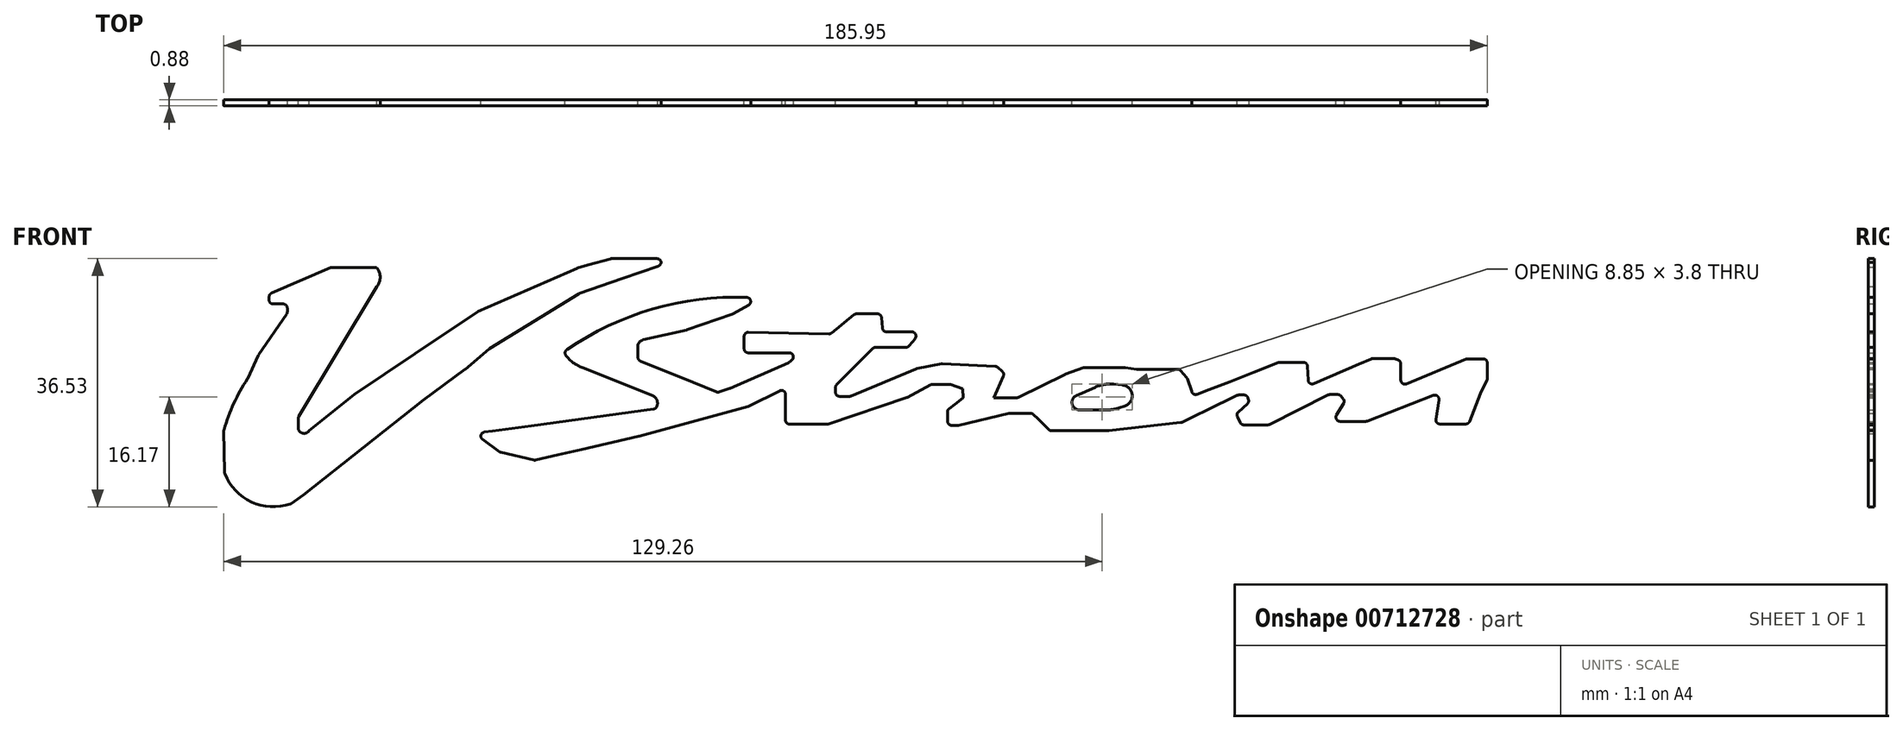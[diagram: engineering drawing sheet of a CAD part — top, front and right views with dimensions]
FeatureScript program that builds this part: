
annotation { "Feature Type Name" : "Feature", "Feature Type Description" : "" }
export const myFeature = defineFeature(function(context is Context, id is Id, definition is map)
    precondition{}
    {
        {
            var Q0;
            Q0=qCreatedBy(makeId("Front.planeOp"),FACE);
            var sketch = newSketch(context, id + "F0", { "sketchPlane" : qUnion([Q0])});
            skLineSegment(sketch, "E0", {"start": v(71.75, 23.37) * mm, "end": v(68, 21.28) * mm});
            skLineSegment(sketch, "E1", {"start": v(68, 21.28) * mm, "end": v(61.86, 19.14) * mm});
            skLineSegment(sketch, "E2", {"start": v(61.86, 19.14) * mm, "end": v(56.05, 17.82) * mm});
            skLineSegment(sketch, "E3", {"start": v(55.28, 16.82) * mm, "end": v(55.32, 15.1) * mm});
            skLineSegment(sketch, "E4", {"start": v(55.32, 15.1) * mm, "end": v(62.67, 12.12) * mm});
            skLineSegment(sketch, "E5", {"start": v(62.67, 12.12) * mm, "end": v(66, 10.76) * mm});
            skLineSegment(sketch, "E6", {"start": v(66, 10.76) * mm, "end": v(67.6, 11.32) * mm});
            skLineSegment(sketch, "E7", {"start": v(67.6, 11.32) * mm, "end": v(75.53, 14.78) * mm});
            skLineSegment(sketch, "E8", {"start": v(75.53, 14.78) * mm, "end": v(77.05, 16.07) * mm});
            skLineSegment(sketch, "E9", {"start": v(77.05, 16.07) * mm, "end": v(69.52, 16.07) * mm});
            skLineSegment(sketch, "E10", {"start": v(69.52, 16.07) * mm, "end": v(69.52, 18.83) * mm});
            skLineSegment(sketch, "E11", {"start": v(69.52, 18.83) * mm, "end": v(81.09, 18.6) * mm});
            skLineSegment(sketch, "E12", {"start": v(81.09, 18.6) * mm, "end": v(84.4, 21.29) * mm});
            skLineSegment(sketch, "E13", {"start": v(84.4, 21.29) * mm, "end": v(87.87, 21.29) * mm});
            skLineSegment(sketch, "E14", {"start": v(87.87, 21.29) * mm, "end": v(88.07, 18.87) * mm});
            skLineSegment(sketch, "E15", {"start": v(88.07, 18.87) * mm, "end": v(93.1, 18.87) * mm});
            skLineSegment(sketch, "E16", {"start": v(93.1, 18.87) * mm, "end": v(91.44, 16.8) * mm});
            skLineSegment(sketch, "E17", {"start": v(91.44, 16.8) * mm, "end": v(86.88, 16.8) * mm});
            skLineSegment(sketch, "E18", {"start": v(86.88, 16.8) * mm, "end": v(81.75, 11.67) * mm});
            skLineSegment(sketch, "E19", {"start": v(81.75, 11.67) * mm, "end": v(81.75, 10.24) * mm});
            skLineSegment(sketch, "E20", {"start": v(81.75, 10.24) * mm, "end": v(83.7, 10.24) * mm});
            skLineSegment(sketch, "E21", {"start": v(83.7, 10.24) * mm, "end": v(92.6, 13.94) * mm});
            skLineSegment(sketch, "E22", {"start": v(92.6, 13.94) * mm, "end": v(95.98, 14.63) * mm});
            skLineSegment(sketch, "E23", {"start": v(95.98, 14.63) * mm, "end": v(103.29, 14.27) * mm});
            skLineSegment(sketch, "E24", {"start": v(103.29, 14.27) * mm, "end": v(104.36, 13.3) * mm});
            skLineSegment(sketch, "E25", {"start": v(104.36, 13.3) * mm, "end": v(103.4, 11.1) * mm});
            skLineSegment(sketch, "E26", {"start": v(103.4, 11.1) * mm, "end": v(102.94, 10.06) * mm});
            skLineSegment(sketch, "E27", {"start": v(102.94, 10.06) * mm, "end": v(103.99, 10.06) * mm});
            skLineSegment(sketch, "E28", {"start": v(103.99, 10.06) * mm, "end": v(106.08, 10.06) * mm});
            skLineSegment(sketch, "E29", {"start": v(106.08, 10.06) * mm, "end": v(112.49, 13.2) * mm});
            skLineSegment(sketch, "E30", {"start": v(112.49, 13.2) * mm, "end": v(115.03, 14.1) * mm});
            skLineSegment(sketch, "E31", {"start": v(115.03, 14.1) * mm, "end": v(118.01, 14.1) * mm});
            skLineSegment(sketch, "E32", {"start": v(118.01, 14.1) * mm, "end": v(120.48, 14.1) * mm});
            skLineSegment(sketch, "E33", {"start": v(120.48, 14.1) * mm, "end": v(122.09, 13.88) * mm});
            skLineSegment(sketch, "E34", {"start": v(-35.24, 14.16) * mm, "end": v(-35.24, 14.16) * mm});
            skLineSegment(sketch, "E35", {"start": v(122.09, 13.88) * mm, "end": v(127.78, 13.88) * mm});
            skLineSegment(sketch, "E36", {"start": v(127.78, 13.88) * mm, "end": v(128.8, 12.7) * mm});
            skLineSegment(sketch, "E37", {"start": v(128.8, 12.7) * mm, "end": v(129.41, 10.9) * mm});
            skLineSegment(sketch, "E38", {"start": v(129.41, 10.9) * mm, "end": v(129.41, 10.23) * mm});
            skLineSegment(sketch, "E39", {"start": v(129.41, 10.23) * mm, "end": v(131.71, 11.13) * mm});
            skLineSegment(sketch, "E40", {"start": v(131.71, 11.13) * mm, "end": v(134.48, 12.2) * mm});
            skLineSegment(sketch, "E41", {"start": v(134.48, 12.2) * mm, "end": v(137.66, 13.45) * mm});
            skLineSegment(sketch, "E42", {"start": v(137.66, 13.45) * mm, "end": v(141.15, 14.8) * mm});
            skLineSegment(sketch, "E43", {"start": v(141.15, 14.8) * mm, "end": v(144.88, 14.8) * mm});
            skLineSegment(sketch, "E44", {"start": v(144.88, 14.8) * mm, "end": v(145, 12.25) * mm});
            skLineSegment(sketch, "E45", {"start": v(145, 12.25) * mm, "end": v(145.02, 11.64) * mm});
            skLineSegment(sketch, "E46", {"start": v(145.02, 11.64) * mm, "end": v(151.78, 14.55) * mm});
            skLineSegment(sketch, "E47", {"start": v(151.78, 14.55) * mm, "end": v(153.53, 15.3) * mm});
            skLineSegment(sketch, "E48", {"start": v(153.53, 15.3) * mm, "end": v(156.55, 15.3) * mm});
            skLineSegment(sketch, "E49", {"start": v(156.55, 15.3) * mm, "end": v(157.39, 14.97) * mm});
            skLineSegment(sketch, "E50", {"start": v(157.39, 14.97) * mm, "end": v(157.39, 12.95) * mm});
            skLineSegment(sketch, "E51", {"start": v(157.39, 12.95) * mm, "end": v(157.39, 12.28) * mm});
            skLineSegment(sketch, "E52", {"start": v(157.39, 12.28) * mm, "end": v(157.39, 11.6) * mm});
            skLineSegment(sketch, "E53", {"start": v(157.39, 11.6) * mm, "end": v(166.26, 15.27) * mm});
            skLineSegment(sketch, "E54", {"start": v(166.26, 15.27) * mm, "end": v(168.95, 15.27) * mm});
            skLineSegment(sketch, "E55", {"start": v(168.95, 15.27) * mm, "end": v(168.95, 12.49) * mm});
            skLineSegment(sketch, "E56", {"start": v(168.95, 12.49) * mm, "end": v(168.03, 10.64) * mm});
            skLineSegment(sketch, "E57", {"start": v(8.4, 22.6) * mm, "end": v(8.4, 21.37) * mm});
            skLineSegment(sketch, "E58", {"start": v(8.4, 21.37) * mm, "end": v(4.54, 15.76) * mm});
            skLineSegment(sketch, "E59", {"start": v(4.54, 15.76) * mm, "end": v(3.07, 12.62) * mm});
            skLineSegment(sketch, "E60", {"start": v(9.86, 7.43) * mm, "end": v(9.86, 5.91) * mm});
            skArc(sketch, "E61", {"start": v(9.86, 6.28) * mm, "mid": v(10.32, 5.35) * mm, "end": v(11.32, 5.64) * mm});
            skLineSegment(sketch, "E62", {"start": v(11.32, 5.64) * mm, "end": v(17.38, 10.52) * mm});
            skLineSegment(sketch, "E63", {"start": v(17.38, 10.52) * mm, "end": v(25.44, 15.92) * mm});
            skLineSegment(sketch, "E64", {"start": v(25.44, 15.92) * mm, "end": v(33.85, 21.57) * mm});
            skLineSegment(sketch, "E65", {"start": v(33.85, 21.57) * mm, "end": v(47.2, 27.4) * mm});
            skLineSegment(sketch, "E66", {"start": v(47.2, 27.4) * mm, "end": v(48.62, 27.8) * mm});
            skLineSegment(sketch, "E67", {"start": v(48.62, 27.8) * mm, "end": v(51.72, 28.68) * mm});
            skLineSegment(sketch, "E68", {"start": v(51.72, 28.68) * mm, "end": v(58.4, 28.68) * mm});
            skLineSegment(sketch, "E69", {"start": v(58.4, 28.68) * mm, "end": v(58.4, 27.8) * mm});
            skLineSegment(sketch, "E70", {"start": v(58.4, 27.8) * mm, "end": v(53.3, 26.05) * mm});
            skLineSegment(sketch, "E71", {"start": v(53.3, 26.05) * mm, "end": v(47.42, 24.02) * mm});
            skLineSegment(sketch, "E72", {"start": v(47.42, 24.02) * mm, "end": v(35.42, 16.61) * mm});
            skLineSegment(sketch, "E73", {"start": v(35.42, 16.61) * mm, "end": v(32.2, 13.86) * mm});
            skLineSegment(sketch, "E74", {"start": v(33.43, 5.28) * mm, "end": v(35.83, 5.6) * mm});
            skLineSegment(sketch, "E75", {"start": v(5.96, 22.6) * mm, "end": v(5.96, 23.91) * mm});
            skLineSegment(sketch, "E76", {"start": v(5.96, 23.91) * mm, "end": v(14.33, 27.5) * mm});
            skLineSegment(sketch, "E77", {"start": v(14.33, 27.5) * mm, "end": v(20.37, 27.5) * mm});
            skLineSegment(sketch, "E78", {"start": v(20.4, 24.92) * mm, "end": v(9.86, 7.43) * mm});
            skLineSegment(sketch, "E79", {"start": v(5.96, 22.6) * mm, "end": v(8.4, 22.6) * mm});
            skArc(sketch, "E80", {"start": v(20.4, 24.92) * mm, "mid": v(20.82, 26.21) * mm, "end": v(20.37, 27.5) * mm});
            skLineSegment(sketch, "E81", {"start": v(57.34, 10.31) * mm, "end": v(47.91, 14.1) * mm});
            skArc(sketch, "E82", {"start": v(45.36, 16.2) * mm, "mid": v(46.45, 14.92) * mm, "end": v(47.91, 14.1) * mm});
            skArc(sketch, "E83", {"start": v(57.64, 8.58) * mm, "mid": v(57.89, 9.64) * mm, "end": v(57.12, 10.4) * mm});
            skLineSegment(sketch, "E84", {"start": v(166.46, 6.55) * mm, "end": v(161.99, 6.55) * mm});
            skLineSegment(sketch, "E85", {"start": v(161.99, 6.55) * mm, "end": v(162.63, 10.72) * mm});
            skLineSegment(sketch, "E86", {"start": v(162.63, 10.72) * mm, "end": v(152.81, 6.9) * mm});
            skLineSegment(sketch, "E87", {"start": v(152.81, 6.9) * mm, "end": v(148.28, 6.9) * mm});
            skLineSegment(sketch, "E88", {"start": v(148.28, 6.9) * mm, "end": v(149.93, 9.6) * mm});
            skLineSegment(sketch, "E89", {"start": v(149.93, 9.6) * mm, "end": v(149.22, 10.48) * mm});
            skLineSegment(sketch, "E90", {"start": v(149.22, 10.48) * mm, "end": v(147.75, 10.48) * mm});
            skLineSegment(sketch, "E91", {"start": v(147.75, 10.48) * mm, "end": v(139.7, 6.43) * mm});
            skLineSegment(sketch, "E92", {"start": v(139.7, 6.43) * mm, "end": v(136.05, 6.43) * mm});
            skLineSegment(sketch, "E93", {"start": v(136.05, 6.43) * mm, "end": v(135.34, 7.9) * mm});
            skLineSegment(sketch, "E94", {"start": v(135.34, 7.9) * mm, "end": v(137.1, 9.49) * mm});
            skLineSegment(sketch, "E95", {"start": v(137.1, 9.49) * mm, "end": v(136.82, 10.43) * mm});
            skLineSegment(sketch, "E96", {"start": v(136.82, 10.43) * mm, "end": v(135.61, 10.43) * mm});
            skLineSegment(sketch, "E97", {"start": v(135.61, 10.43) * mm, "end": v(131.41, 8.4) * mm});
            skLineSegment(sketch, "E98", {"start": v(131.41, 8.4) * mm, "end": v(129.95, 7.68) * mm});
            skLineSegment(sketch, "E99", {"start": v(129.95, 7.68) * mm, "end": v(128.02, 6.75) * mm});
            skLineSegment(sketch, "E100", {"start": v(128.02, 6.75) * mm, "end": v(121.39, 6) * mm});
            skLineSegment(sketch, "E101", {"start": v(121.39, 6) * mm, "end": v(118.26, 5.64) * mm});
            skLineSegment(sketch, "E102", {"start": v(118.26, 5.64) * mm, "end": v(112.75, 5.64) * mm});
            skLineSegment(sketch, "E103", {"start": v(112.75, 5.64) * mm, "end": v(110.45, 5.64) * mm});
            skLineSegment(sketch, "E104", {"start": v(110.45, 5.64) * mm, "end": v(108.8, 7.27) * mm});
            skLineSegment(sketch, "E105", {"start": v(108.8, 7.27) * mm, "end": v(108.1, 7.96) * mm});
            skLineSegment(sketch, "E106", {"start": v(108.1, 7.96) * mm, "end": v(107.3, 7.96) * mm});
            skLineSegment(sketch, "E107", {"start": v(107.3, 7.96) * mm, "end": v(105.01, 7.96) * mm});
            skLineSegment(sketch, "E108", {"start": v(105.01, 7.96) * mm, "end": v(98.13, 6.37) * mm});
            skLineSegment(sketch, "E109", {"start": v(98.13, 6.37) * mm, "end": v(96.74, 6.37) * mm});
            skLineSegment(sketch, "E110", {"start": v(96.74, 6.37) * mm, "end": v(96.74, 8.45) * mm});
            skLineSegment(sketch, "E111", {"start": v(96.74, 8.45) * mm, "end": v(97.7, 9.2) * mm});
            skLineSegment(sketch, "E112", {"start": v(97.7, 9.2) * mm, "end": v(98.82, 10.04) * mm});
            skLineSegment(sketch, "E113", {"start": v(98.82, 10.04) * mm, "end": v(98.77, 11.27) * mm});
            skLineSegment(sketch, "E114", {"start": v(98.77, 11.27) * mm, "end": v(97.06, 11.86) * mm});
            skLineSegment(sketch, "E115", {"start": v(97.06, 11.86) * mm, "end": v(94.56, 11.86) * mm});
            skLineSegment(sketch, "E116", {"start": v(94.56, 11.86) * mm, "end": v(91.36, 10.1) * mm});
            skLineSegment(sketch, "E117", {"start": v(91.36, 10.1) * mm, "end": v(80.65, 6.52) * mm});
            skLineSegment(sketch, "E118", {"start": v(80.65, 6.52) * mm, "end": v(77.45, 6.52) * mm});
            skLineSegment(sketch, "E119", {"start": v(77.45, 6.52) * mm, "end": v(75.05, 6.52) * mm});
            skLineSegment(sketch, "E120", {"start": v(75.05, 6.52) * mm, "end": v(75.05, 11.05) * mm});
            skLineSegment(sketch, "E121", {"start": v(75.05, 11.05) * mm, "end": v(74.4, 11.05) * mm});
            skLineSegment(sketch, "E122", {"start": v(74.4, 11.05) * mm, "end": v(70.14, 8.92) * mm});
            skLineSegment(sketch, "E123", {"start": v(70.14, 8.92) * mm, "end": v(55.44, 4.9) * mm});
            skLineSegment(sketch, "E124", {"start": v(55.44, 4.9) * mm, "end": v(47.76, 3.13) * mm});
            skLineSegment(sketch, "E125", {"start": v(47.76, 3.13) * mm, "end": v(44.61, 2.4) * mm});
            skLineSegment(sketch, "E126", {"start": v(44.61, 2.4) * mm, "end": v(41.52, 1.69) * mm});
            skLineSegment(sketch, "E127", {"start": v(41.52, 1.69) * mm, "end": v(36.86, 2.77) * mm});
            skLineSegment(sketch, "E128", {"start": v(36.86, 2.77) * mm, "end": v(33.43, 5.28) * mm});
            skLineSegment(sketch, "E129", {"start": v(-0.1, 5.7) * mm, "end": v(0, 0) * mm});
            skLineSegment(sketch, "E130", {"start": v(26.6, 9.77) * mm, "end": v(10.57, -2.96) * mm});
            skLineSegment(sketch, "E131", {"start": v(10.57, -2.96) * mm, "end": v(8.9, -4.11) * mm});
            skLineSegment(sketch, "E132", {"start": v(41.05, 6.32) * mm, "end": v(57.64, 8.58) * mm});
            skLineSegment(sketch, "E133", {"start": v(168.03, 10.64) * mm, "end": v(166.46, 6.55) * mm});
            skArc(sketch, "E134", {"start": v(3.07, 12.62) * mm, "mid": v(1.23, 9.28) * mm, "end": v(-0.1, 5.7) * mm});
            skLineSegment(sketch, "E135", {"start": v(32.2, 13.86) * mm, "end": v(26.6, 9.77) * mm});
            skLineSegment(sketch, "E136", {"start": v(41.05, 6.32) * mm, "end": v(35.83, 5.6) * mm});
            skArc(sketch, "E137", {"start": v(113.98, 10.35) * mm, "mid": v(113.4, 9.23) * mm, "end": v(114.38, 8.44) * mm});
            skLineSegment(sketch, "E138", {"start": v(113.98, 10.35) * mm, "end": v(116.47, 11.46) * mm});
            skLineSegment(sketch, "E139", {"start": v(114.38, 8.44) * mm, "end": v(118.08, 8.44) * mm});
            skArc(sketch, "E140", {"start": v(120.48, 8.98) * mm, "mid": v(121.44, 10.5) * mm, "end": v(120.14, 11.77) * mm});
            skLineSegment(sketch, "E141", {"start": v(118.97, 11.88) * mm, "end": v(120.14, 11.77) * mm});
            skLineSegment(sketch, "E142", {"start": v(119.72, 8.71) * mm, "end": v(120.48, 8.98) * mm});
            skPoint(sketch, "E143.visualSharp", {"position": v(117.67, 12) * mm});
            skArc(sketch, "E143.filletArc", {"start": v(118.97, 11.88) * mm, "mid": v(117.7, 11.83) * mm, "end": v(116.47, 11.46) * mm});
            skPoint(sketch, "E144.visualSharp", {"position": v(118.92, 8.44) * mm});
            skArc(sketch, "E144.filletArc", {"start": v(118.08, 8.44) * mm, "mid": v(118.91, 8.5) * mm, "end": v(119.72, 8.71) * mm});
            skArc(sketch, "E145", {"start": v(71.75, 23.37) * mm, "mid": v(57.92, 22.11) * mm, "end": v(45.36, 16.2) * mm});
            skPoint(sketch, "E146.visualSharp", {"position": v(55.25, 17.64) * mm});
            skArc(sketch, "E146.filletArc", {"start": v(56.05, 17.82) * mm, "mid": v(55.49, 17.46) * mm, "end": v(55.28, 16.82) * mm});
            skArc(sketch, "E147", {"start": v(0, 0) * mm, "mid": v(3.6, -3.89) * mm, "end": v(8.9, -4.11) * mm});
            skSolve(sketch);
        }
        {
            var Q0;
            Q0=qSketchRegion(id+"F0",true);
            extrude(context, id + "F1", {"entities" : qUnion([Q0]), "depth" : .8 * mm, "offsetDistance" : 25 * mm});
        }
        {
            var Q0;
            Q0=makeQuery(id+"F1.opExtrude","SWEPT_BODY",BODY,{"disambiguationData":[OSD([sQuery(id+"F0.wireOp",EDGE,"241e14e1-87a1-43d8-a896-4ed85162aa12"),sQuery(id+"F0.wireOp",EDGE,"f7f46965-fdce-40b1-8a69-0ea02161d450"),sQuery(id+"F0.wireOp",EDGE,"a256f486-1147-4e8e-9624-e69cd99640f2"),sQuery(id+"F0.wireOp",EDGE,"E0"),sQuery(id+"F0.wireOp",EDGE,"E1"),sQuery(id+"F0.wireOp",EDGE,"E2"),sQuery(id+"F0.wireOp",EDGE,"E3"),sQuery(id+"F0.wireOp",EDGE,"E4"),sQuery(id+"F0.wireOp",EDGE,"E5"),sQuery(id+"F0.wireOp",EDGE,"E6"),sQuery(id+"F0.wireOp",EDGE,"E7"),sQuery(id+"F0.wireOp",EDGE,"E8"),sQuery(id+"F0.wireOp",EDGE,"E9"),sQuery(id+"F0.wireOp",EDGE,"E10"),sQuery(id+"F0.wireOp",EDGE,"E11"),sQuery(id+"F0.wireOp",EDGE,"E12"),sQuery(id+"F0.wireOp",EDGE,"E13"),sQuery(id+"F0.wireOp",EDGE,"E14"),sQuery(id+"F0.wireOp",EDGE,"E15"),sQuery(id+"F0.wireOp",EDGE,"E16"),sQuery(id+"F0.wireOp",EDGE,"E17"),sQuery(id+"F0.wireOp",EDGE,"E18"),sQuery(id+"F0.wireOp",EDGE,"E19"),sQuery(id+"F0.wireOp",EDGE,"E20"),sQuery(id+"F0.wireOp",EDGE,"E21"),sQuery(id+"F0.wireOp",EDGE,"E22"),sQuery(id+"F0.wireOp",EDGE,"E23"),sQuery(id+"F0.wireOp",EDGE,"E24"),sQuery(id+"F0.wireOp",EDGE,"E25"),sQuery(id+"F0.wireOp",EDGE,"E26"),sQuery(id+"F0.wireOp",EDGE,"E27"),sQuery(id+"F0.wireOp",EDGE,"E28"),sQuery(id+"F0.wireOp",EDGE,"E29"),sQuery(id+"F0.wireOp",EDGE,"E30"),sQuery(id+"F0.wireOp",EDGE,"E31"),sQuery(id+"F0.wireOp",EDGE,"E32"),sQuery(id+"F0.wireOp",EDGE,"E33"),sQuery(id+"F0.wireOp",EDGE,"24c02880-417f-4c24-b8b8-f4173c506c8a"),sQuery(id+"F0.wireOp",EDGE,"c1167789-1dd6-4c8a-b9db-14aab257ee89"),sQuery(id+"F0.wireOp",EDGE,"97e02e69-64ad-4fc2-ba99-ada5d7f4203f"),sQuery(id+"F0.wireOp",EDGE,"a728134e-6b61-4dc4-b5d7-6c3bc719696b"),sQuery(id+"F0.wireOp",EDGE,"03a7d401-13a4-461c-8d26-49e58f535fc3"),sQuery(id+"F0.wireOp",EDGE,"a3bd3416-707c-4540-b944-4694eed28f36"),sQuery(id+"F0.wireOp",EDGE,"ae496998-b544-44f2-afee-4042db2af114"),sQuery(id+"F0.wireOp",EDGE,"d8a8be79-a09e-4068-9526-32c7dd8d4367"),sQuery(id+"F0.wireOp",EDGE,"6c9cf376-8706-417d-a2f8-7997adb0d334"),sQuery(id+"F0.wireOp",EDGE,"4fed2303-0bfb-4ab1-8d0b-459c1d0f22cc"),sQuery(id+"F0.wireOp",EDGE,"54fe9d9b-3ee6-47e4-8d7e-fb489f7f2c80"),sQuery(id+"F0.wireOp",EDGE,"767a3e55-a90d-4037-a153-983baa27fcb7"),sQuery(id+"F0.wireOp",EDGE,"E35"),sQuery(id+"F0.wireOp",EDGE,"E36"),sQuery(id+"F0.wireOp",EDGE,"E37"),sQuery(id+"F0.wireOp",EDGE,"E38"),sQuery(id+"F0.wireOp",EDGE,"E39"),sQuery(id+"F0.wireOp",EDGE,"E40"),sQuery(id+"F0.wireOp",EDGE,"E41"),sQuery(id+"F0.wireOp",EDGE,"E42"),sQuery(id+"F0.wireOp",EDGE,"E43"),sQuery(id+"F0.wireOp",EDGE,"E44"),sQuery(id+"F0.wireOp",EDGE,"E45"),sQuery(id+"F0.wireOp",EDGE,"E46"),sQuery(id+"F0.wireOp",EDGE,"E47"),sQuery(id+"F0.wireOp",EDGE,"E48"),sQuery(id+"F0.wireOp",EDGE,"E49"),sQuery(id+"F0.wireOp",EDGE,"E50"),sQuery(id+"F0.wireOp",EDGE,"E51"),sQuery(id+"F0.wireOp",EDGE,"E52"),sQuery(id+"F0.wireOp",EDGE,"E53"),sQuery(id+"F0.wireOp",EDGE,"E54"),sQuery(id+"F0.wireOp",EDGE,"E55"),sQuery(id+"F0.wireOp",EDGE,"E56"),sQuery(id+"F0.wireOp",EDGE,"E57"),sQuery(id+"F0.wireOp",EDGE,"E58"),sQuery(id+"F0.wireOp",EDGE,"E59"),sQuery(id+"F0.wireOp",EDGE,"E60"),sQuery(id+"F0.wireOp",EDGE,"E61"),sQuery(id+"F0.wireOp",EDGE,"E62"),sQuery(id+"F0.wireOp",EDGE,"E63"),sQuery(id+"F0.wireOp",EDGE,"E64"),sQuery(id+"F0.wireOp",EDGE,"E65"),sQuery(id+"F0.wireOp",EDGE,"E66"),sQuery(id+"F0.wireOp",EDGE,"E67"),sQuery(id+"F0.wireOp",EDGE,"E68"),sQuery(id+"F0.wireOp",EDGE,"E69"),sQuery(id+"F0.wireOp",EDGE,"E70"),sQuery(id+"F0.wireOp",EDGE,"E71"),sQuery(id+"F0.wireOp",EDGE,"E72"),sQuery(id+"F0.wireOp",EDGE,"E73"),sQuery(id+"F0.wireOp",EDGE,"377fbeee-e580-4fd5-9061-dc16fb011731"),sQuery(id+"F0.wireOp",EDGE,"38df82f0-7285-487d-a951-3b541ab7109e"),sQuery(id+"F0.wireOp",EDGE,"E74"),sQuery(id+"F0.wireOp",EDGE,"6855bdf4-7372-49db-ac6e-076a8d5753c6"),sQuery(id+"F0.wireOp",EDGE,"e5794261-fd4b-449f-95b0-f2c794a3797c"),sQuery(id+"F0.wireOp",EDGE,"816a1e28-1c5c-4fd2-90ff-496e4fceb872"),sQuery(id+"F0.wireOp",EDGE,"E75"),sQuery(id+"F0.wireOp",EDGE,"E76"),sQuery(id+"F0.wireOp",EDGE,"E77"),sQuery(id+"F0.wireOp",EDGE,"E78"),sQuery(id+"F0.wireOp",EDGE,"E79"),sQuery(id+"F0.wireOp",EDGE,"E80"),sQuery(id+"F0.wireOp",EDGE,"E81"),sQuery(id+"F0.wireOp",EDGE,"d8fff456-97c2-412e-a261-d120211664d1"),sQuery(id+"F0.wireOp",EDGE,"b8273a3d-b15c-450d-bf57-9129b1064c63"),sQuery(id+"F0.wireOp",EDGE,"24f56637-c8b3-4da3-a569-8d1f01dfcf72"),sQuery(id+"F0.wireOp",EDGE,"f2871ee9-4b7f-4278-88fc-bea5587f1b5c"),sQuery(id+"F0.wireOp",EDGE,"E82"),sQuery(id+"F0.wireOp",EDGE,"E83"),sQuery(id+"F0.wireOp",EDGE,"E84"),sQuery(id+"F0.wireOp",EDGE,"E85"),sQuery(id+"F0.wireOp",EDGE,"E86"),sQuery(id+"F0.wireOp",EDGE,"E87"),sQuery(id+"F0.wireOp",EDGE,"E88"),sQuery(id+"F0.wireOp",EDGE,"E89"),sQuery(id+"F0.wireOp",EDGE,"E90"),sQuery(id+"F0.wireOp",EDGE,"E91"),sQuery(id+"F0.wireOp",EDGE,"E92"),sQuery(id+"F0.wireOp",EDGE,"E93"),sQuery(id+"F0.wireOp",EDGE,"E94"),sQuery(id+"F0.wireOp",EDGE,"E95"),sQuery(id+"F0.wireOp",EDGE,"E96"),sQuery(id+"F0.wireOp",EDGE,"E97"),sQuery(id+"F0.wireOp",EDGE,"E98"),sQuery(id+"F0.wireOp",EDGE,"E99"),sQuery(id+"F0.wireOp",EDGE,"E100"),sQuery(id+"F0.wireOp",EDGE,"E101"),sQuery(id+"F0.wireOp",EDGE,"E102"),sQuery(id+"F0.wireOp",EDGE,"E103"),sQuery(id+"F0.wireOp",EDGE,"E104"),sQuery(id+"F0.wireOp",EDGE,"E105"),sQuery(id+"F0.wireOp",EDGE,"E106"),sQuery(id+"F0.wireOp",EDGE,"E107"),sQuery(id+"F0.wireOp",EDGE,"E108"),sQuery(id+"F0.wireOp",EDGE,"E109"),sQuery(id+"F0.wireOp",EDGE,"E110"),sQuery(id+"F0.wireOp",EDGE,"E111"),sQuery(id+"F0.wireOp",EDGE,"E112"),sQuery(id+"F0.wireOp",EDGE,"E113"),sQuery(id+"F0.wireOp",EDGE,"E114"),sQuery(id+"F0.wireOp",EDGE,"E115"),sQuery(id+"F0.wireOp",EDGE,"E116"),sQuery(id+"F0.wireOp",EDGE,"E117"),sQuery(id+"F0.wireOp",EDGE,"E118"),sQuery(id+"F0.wireOp",EDGE,"E119"),sQuery(id+"F0.wireOp",EDGE,"E120"),sQuery(id+"F0.wireOp",EDGE,"E121"),sQuery(id+"F0.wireOp",EDGE,"E122"),sQuery(id+"F0.wireOp",EDGE,"E123"),sQuery(id+"F0.wireOp",EDGE,"E124"),sQuery(id+"F0.wireOp",EDGE,"E125"),sQuery(id+"F0.wireOp",EDGE,"E126"),sQuery(id+"F0.wireOp",EDGE,"E127"),sQuery(id+"F0.wireOp",EDGE,"E128"),sQuery(id+"F0.wireOp",EDGE,"E129"),sQuery(id+"F0.wireOp",EDGE,"dab5b0ac-2ca5-47d6-9900-db6adb9d8108"),sQuery(id+"F0.wireOp",EDGE,"b405192e-a51a-4a0c-819a-7e94ddbcd1a0"),sQuery(id+"F0.wireOp",EDGE,"de686d96-7963-4258-8ff2-fc4ca0e2d47a"),sQuery(id+"F0.wireOp",EDGE,"c7cd1295-3dc0-4c06-b4a5-3722ac70a722"),sQuery(id+"F0.wireOp",EDGE,"96680c50-dba8-4e0d-9e03-9b80bdf2aefb"),sQuery(id+"F0.wireOp",EDGE,"E130"),sQuery(id+"F0.wireOp",EDGE,"E131"),sQuery(id+"F0.wireOp",EDGE,"E132"),sQuery(id+"F0.wireOp",EDGE,"E133"),sQuery(id+"F0.wireOp",EDGE,"E134")])]});
            var Q1;
            Q1=makeQuery(id+"F1.opExtrude","SWEPT_BODY",BODY,{"disambiguationData":[OSD([sQuery(id+"F0.wireOp",EDGE,"E57"),sQuery(id+"F0.wireOp",EDGE,"E58"),sQuery(id+"F0.wireOp",EDGE,"E59"),sQuery(id+"F0.wireOp",EDGE,"E60"),sQuery(id+"F0.wireOp",EDGE,"E61"),sQuery(id+"F0.wireOp",EDGE,"E62"),sQuery(id+"F0.wireOp",EDGE,"E63"),sQuery(id+"F0.wireOp",EDGE,"E64"),sQuery(id+"F0.wireOp",EDGE,"E65"),sQuery(id+"F0.wireOp",EDGE,"E66"),sQuery(id+"F0.wireOp",EDGE,"E67"),sQuery(id+"F0.wireOp",EDGE,"E68"),sQuery(id+"F0.wireOp",EDGE,"E69"),sQuery(id+"F0.wireOp",EDGE,"E70"),sQuery(id+"F0.wireOp",EDGE,"E71"),sQuery(id+"F0.wireOp",EDGE,"E72"),sQuery(id+"F0.wireOp",EDGE,"E73"),sQuery(id+"F0.wireOp",EDGE,"6855bdf4-7372-49db-ac6e-076a8d5753c6"),sQuery(id+"F0.wireOp",EDGE,"e5794261-fd4b-449f-95b0-f2c794a3797c"),sQuery(id+"F0.wireOp",EDGE,"816a1e28-1c5c-4fd2-90ff-496e4fceb872"),sQuery(id+"F0.wireOp",EDGE,"E75"),sQuery(id+"F0.wireOp",EDGE,"E76"),sQuery(id+"F0.wireOp",EDGE,"E77"),sQuery(id+"F0.wireOp",EDGE,"E78"),sQuery(id+"F0.wireOp",EDGE,"E79"),sQuery(id+"F0.wireOp",EDGE,"E80"),sQuery(id+"F0.wireOp",EDGE,"E129"),sQuery(id+"F0.wireOp",EDGE,"E130"),sQuery(id+"F0.wireOp",EDGE,"E131"),sQuery(id+"F0.wireOp",EDGE,"E134"),sQuery(id+"F0.wireOp",EDGE,"E135")])]});
            var Q2;
            Q2=makeQuery(id+"F1.opExtrude","CAP_VERTEX",VERTEX,{"disambiguationData":[OSD([sQuery(id+"F0.wireOp",EDGE,"E75"),sQuery(id+"F0.wireOp",EDGE,"E76")])],"isStart":false});
            transform(context, id + "F2", {"entities" : qUnion([Q0, Q1]), "transformType" : TransformType.SCALE_UNIFORMLY, "scale" : 1.1, "scalePoint" : qUnion([Q2]), "makeCopy" : false});
        }
        {
            var Q0;
            Q0=makeQuery(id+"F1.opExtrude","SWEPT_EDGE",EDGE,{"disambiguationData":[OSD([sQuery(id+"F0.wireOp",EDGE,"e5794261-fd4b-449f-95b0-f2c794a3797c"),sQuery(id+"F0.wireOp",EDGE,"E129")])]});
            var Q1;
            Q1=makeQuery(id+"F1.opExtrude","SWEPT_EDGE",EDGE,{"disambiguationData":[OSD([sQuery(id+"F0.wireOp",EDGE,"E129"),sQuery(id+"F0.wireOp",EDGE,"E134")])]});
            var Q2;
            Q2=makeQuery(id+"F1.opExtrude","SWEPT_EDGE",EDGE,{"disambiguationData":[OSD([sQuery(id+"F0.wireOp",EDGE,"e5794261-fd4b-449f-95b0-f2c794a3797c"),sQuery(id+"F0.wireOp",EDGE,"816a1e28-1c5c-4fd2-90ff-496e4fceb872")])]});
            var Q3;
            Q3=makeQuery(id+"F1.opExtrude","SWEPT_EDGE",EDGE,{"disambiguationData":[OSD([sQuery(id+"F0.wireOp",EDGE,"6855bdf4-7372-49db-ac6e-076a8d5753c6"),sQuery(id+"F0.wireOp",EDGE,"E131")])]});
            var Q4;
            Q4=makeQuery(id+"F1.opExtrude","SWEPT_EDGE",EDGE,{"disambiguationData":[OSD([sQuery(id+"F0.wireOp",EDGE,"E60"),sQuery(id+"F0.wireOp",EDGE,"E78")])]});
            var Q5;
            Q5=makeQuery(id+"F1.opExtrude","SWEPT_EDGE",EDGE,{"disambiguationData":[OSD([sQuery(id+"F0.wireOp",EDGE,"E57"),sQuery(id+"F0.wireOp",EDGE,"E58")])]});
            var Q6;
            Q6=makeQuery(id+"F1.opExtrude","SWEPT_EDGE",EDGE,{"disambiguationData":[OSD([sQuery(id+"F0.wireOp",EDGE,"E57"),sQuery(id+"F0.wireOp",EDGE,"E79")])]});
            var Q7;
            Q7=makeQuery(id+"F1.opExtrude","SWEPT_EDGE",EDGE,{"disambiguationData":[OSD([sQuery(id+"F0.wireOp",EDGE,"E75"),sQuery(id+"F0.wireOp",EDGE,"E79")])]});
            var Q8;
            Q8=makeQuery(id+"F1.opExtrude","SWEPT_EDGE",EDGE,{"disambiguationData":[OSD([sQuery(id+"F0.wireOp",EDGE,"E75"),sQuery(id+"F0.wireOp",EDGE,"E76")])]});
            var Q9;
            Q9=makeQuery(id+"F1.opExtrude","SWEPT_EDGE",EDGE,{"disambiguationData":[OSD([sQuery(id+"F0.wireOp",EDGE,"E76"),sQuery(id+"F0.wireOp",EDGE,"E77")])]});
            var Q10;
            Q10=makeQuery(id+"F1.opExtrude","SWEPT_EDGE",EDGE,{"disambiguationData":[OSD([sQuery(id+"F0.wireOp",EDGE,"E77"),sQuery(id+"F0.wireOp",EDGE,"E80")])]});
            var Q11;
            Q11=makeQuery(id+"F1.opExtrude","SWEPT_EDGE",EDGE,{"disambiguationData":[OSD([sQuery(id+"F0.wireOp",EDGE,"E69"),sQuery(id+"F0.wireOp",EDGE,"E70")])]});
            var Q12;
            Q12=makeQuery(id+"F1.opExtrude","SWEPT_EDGE",EDGE,{"disambiguationData":[OSD([sQuery(id+"F0.wireOp",EDGE,"E72"),sQuery(id+"F0.wireOp",EDGE,"E73")])]});
            var Q13;
            Q13=makeQuery(id+"F1.opExtrude","SWEPT_EDGE",EDGE,{"disambiguationData":[OSD([sQuery(id+"F0.wireOp",EDGE,"E71"),sQuery(id+"F0.wireOp",EDGE,"E72")])]});
            var Q14;
            Q14=makeQuery(id+"F1.opExtrude","SWEPT_EDGE",EDGE,{"disambiguationData":[OSD([sQuery(id+"F0.wireOp",EDGE,"E73"),sQuery(id+"F0.wireOp",EDGE,"E135")])]});
            var Q15;
            Q15=makeQuery(id+"F1.opExtrude","SWEPT_EDGE",EDGE,{"disambiguationData":[OSD([sQuery(id+"F0.wireOp",EDGE,"E130"),sQuery(id+"F0.wireOp",EDGE,"E135")])]});
            var Q16;
            Q16=makeQuery(id+"F1.opExtrude","SWEPT_EDGE",EDGE,{"disambiguationData":[OSD([sQuery(id+"F0.wireOp",EDGE,"E130"),sQuery(id+"F0.wireOp",EDGE,"E131")])]});
            var Q17;
            Q17=makeQuery(id+"F1.opExtrude","SWEPT_EDGE",EDGE,{"disambiguationData":[OSD([sQuery(id+"F0.wireOp",EDGE,"E70"),sQuery(id+"F0.wireOp",EDGE,"E71")])]});
            var Q18;
            Q18=makeQuery(id+"F1.opExtrude","SWEPT_EDGE",EDGE,{"disambiguationData":[OSD([sQuery(id+"F0.wireOp",EDGE,"E62"),sQuery(id+"F0.wireOp",EDGE,"E63")])]});
            var Q19;
            Q19=makeQuery(id+"F1.opExtrude","SWEPT_EDGE",EDGE,{"disambiguationData":[OSD([sQuery(id+"F0.wireOp",EDGE,"E64"),sQuery(id+"F0.wireOp",EDGE,"E65")])]});
            var Q20;
            Q20=makeQuery(id+"F1.opExtrude","SWEPT_EDGE",EDGE,{"disambiguationData":[OSD([sQuery(id+"F0.wireOp",EDGE,"E65"),sQuery(id+"F0.wireOp",EDGE,"E66")])]});
            var Q21;
            Q21=makeQuery(id+"F1.opExtrude","SWEPT_EDGE",EDGE,{"disambiguationData":[OSD([sQuery(id+"F0.wireOp",EDGE,"E67"),sQuery(id+"F0.wireOp",EDGE,"E68")])]});
            var Q22;
            Q22=makeQuery(id+"F1.opExtrude","SWEPT_EDGE",EDGE,{"disambiguationData":[OSD([sQuery(id+"F0.wireOp",EDGE,"E58"),sQuery(id+"F0.wireOp",EDGE,"E59")])]});
            var Q23;
            Q23=makeQuery(id+"F1.opExtrude","SWEPT_EDGE",EDGE,{"disambiguationData":[OSD([sQuery(id+"F0.wireOp",EDGE,"E59"),sQuery(id+"F0.wireOp",EDGE,"E134")])]});
            var Q24;
            Q24=makeQuery(id+"F1.opExtrude","SWEPT_EDGE",EDGE,{"disambiguationData":[OSD([sQuery(id+"F0.wireOp",EDGE,"6855bdf4-7372-49db-ac6e-076a8d5753c6"),sQuery(id+"F0.wireOp",EDGE,"816a1e28-1c5c-4fd2-90ff-496e4fceb872")])]});
            var Q25;
            Q25=makeQuery(id+"F1.opExtrude","SWEPT_EDGE",EDGE,{"disambiguationData":[OSD([sQuery(id+"F0.wireOp",EDGE,"E68"),sQuery(id+"F0.wireOp",EDGE,"E69")])]});
            fillet(context, id + "F3", {"entities" : qUnion([Q0, Q1, Q2, Q3, Q4, Q5, Q6, Q7, Q8, Q9, Q10, Q11, Q12, Q13, Q14, Q15, Q16, Q17, Q18, Q19, Q20, Q21, Q22, Q23, Q24, Q25]), "radius" : .6 * mm, "tangentPropagation" : true, "allowEdgeOverflow" : false});
        }
        {
            var Q0;
            Q0=makeQuery(id+"F1.opExtrude","SWEPT_EDGE",EDGE,{"disambiguationData":[OSD([sQuery(id+"F0.wireOp",EDGE,"d8fff456-97c2-412e-a261-d120211664d1"),sQuery(id+"F0.wireOp",EDGE,"E82")])]});
            var Q1;
            Q1=makeQuery(id+"F1.opExtrude","SWEPT_EDGE",EDGE,{"disambiguationData":[OSD([sQuery(id+"F0.wireOp",EDGE,"E81"),sQuery(id+"F0.wireOp",EDGE,"E82")])]});
            var Q2;
            Q2=makeQuery(id+"F1.opExtrude","SWEPT_EDGE",EDGE,{"disambiguationData":[OSD([sQuery(id+"F0.wireOp",EDGE,"E81"),sQuery(id+"F0.wireOp",EDGE,"E83")])]});
            var Q3;
            Q3=makeQuery(id+"F1.opExtrude","SWEPT_EDGE",EDGE,{"disambiguationData":[OSD([sQuery(id+"F0.wireOp",EDGE,"E74"),sQuery(id+"F0.wireOp",EDGE,"E128")])]});
            var Q4;
            Q4=makeQuery(id+"F1.opExtrude","SWEPT_EDGE",EDGE,{"disambiguationData":[OSD([sQuery(id+"F0.wireOp",EDGE,"E132"),sQuery(id+"F0.wireOp",EDGE,"E136")])]});
            var Q5;
            Q5=makeQuery(id+"F1.opExtrude","SWEPT_EDGE",EDGE,{"disambiguationData":[OSD([sQuery(id+"F0.wireOp",EDGE,"E127"),sQuery(id+"F0.wireOp",EDGE,"E128")])]});
            var Q6;
            Q6=makeQuery(id+"F1.opExtrude","SWEPT_EDGE",EDGE,{"disambiguationData":[OSD([sQuery(id+"F0.wireOp",EDGE,"d8fff456-97c2-412e-a261-d120211664d1"),sQuery(id+"F0.wireOp",EDGE,"b8273a3d-b15c-450d-bf57-9129b1064c63")])]});
            var Q7;
            Q7=makeQuery(id+"F1.opExtrude","SWEPT_EDGE",EDGE,{"disambiguationData":[OSD([sQuery(id+"F0.wireOp",EDGE,"b8273a3d-b15c-450d-bf57-9129b1064c63"),sQuery(id+"F0.wireOp",EDGE,"24f56637-c8b3-4da3-a569-8d1f01dfcf72")])]});
            var Q8;
            Q8=makeQuery(id+"F1.opExtrude","SWEPT_EDGE",EDGE,{"disambiguationData":[OSD([sQuery(id+"F0.wireOp",EDGE,"24f56637-c8b3-4da3-a569-8d1f01dfcf72"),sQuery(id+"F0.wireOp",EDGE,"f2871ee9-4b7f-4278-88fc-bea5587f1b5c")])]});
            var Q9;
            Q9=makeQuery(id+"F1.opExtrude","SWEPT_EDGE",EDGE,{"disambiguationData":[OSD([sQuery(id+"F0.wireOp",EDGE,"241e14e1-87a1-43d8-a896-4ed85162aa12"),sQuery(id+"F0.wireOp",EDGE,"f2871ee9-4b7f-4278-88fc-bea5587f1b5c")])]});
            var Q10;
            Q10=makeQuery(id+"F1.opExtrude","SWEPT_EDGE",EDGE,{"disambiguationData":[OSD([sQuery(id+"F0.wireOp",EDGE,"241e14e1-87a1-43d8-a896-4ed85162aa12"),sQuery(id+"F0.wireOp",EDGE,"f7f46965-fdce-40b1-8a69-0ea02161d450")])]});
            var Q11;
            Q11=makeQuery(id+"F1.opExtrude","SWEPT_EDGE",EDGE,{"disambiguationData":[OSD([sQuery(id+"F0.wireOp",EDGE,"a256f486-1147-4e8e-9624-e69cd99640f2"),sQuery(id+"F0.wireOp",EDGE,"E0")])]});
            var Q12;
            Q12=makeQuery(id+"F1.opExtrude","SWEPT_EDGE",EDGE,{"disambiguationData":[OSD([sQuery(id+"F0.wireOp",EDGE,"E0"),sQuery(id+"F0.wireOp",EDGE,"E1")])]});
            var Q13;
            Q13=makeQuery(id+"F1.opExtrude","SWEPT_EDGE",EDGE,{"disambiguationData":[OSD([sQuery(id+"F0.wireOp",EDGE,"E1"),sQuery(id+"F0.wireOp",EDGE,"E2")])]});
            var Q14;
            Q14=makeQuery(id+"F1.opExtrude","SWEPT_EDGE",EDGE,{"disambiguationData":[OSD([sQuery(id+"F0.wireOp",EDGE,"E2"),sQuery(id+"F0.wireOp",EDGE,"E3")])]});
            var Q15;
            Q15=makeQuery(id+"F1.opExtrude","SWEPT_EDGE",EDGE,{"disambiguationData":[OSD([sQuery(id+"F0.wireOp",EDGE,"E3"),sQuery(id+"F0.wireOp",EDGE,"E4")])]});
            var Q16;
            Q16=makeQuery(id+"F1.opExtrude","SWEPT_EDGE",EDGE,{"disambiguationData":[OSD([sQuery(id+"F0.wireOp",EDGE,"E4"),sQuery(id+"F0.wireOp",EDGE,"E5")])]});
            var Q17;
            Q17=makeQuery(id+"F1.opExtrude","SWEPT_EDGE",EDGE,{"disambiguationData":[OSD([sQuery(id+"F0.wireOp",EDGE,"E5"),sQuery(id+"F0.wireOp",EDGE,"E6")])]});
            var Q18;
            Q18=makeQuery(id+"F1.opExtrude","SWEPT_EDGE",EDGE,{"disambiguationData":[OSD([sQuery(id+"F0.wireOp",EDGE,"E6"),sQuery(id+"F0.wireOp",EDGE,"E7")])]});
            var Q19;
            Q19=makeQuery(id+"F1.opExtrude","SWEPT_EDGE",EDGE,{"disambiguationData":[OSD([sQuery(id+"F0.wireOp",EDGE,"E7"),sQuery(id+"F0.wireOp",EDGE,"E8")])]});
            var Q20;
            Q20=makeQuery(id+"F1.opExtrude","SWEPT_EDGE",EDGE,{"disambiguationData":[OSD([sQuery(id+"F0.wireOp",EDGE,"E10"),sQuery(id+"F0.wireOp",EDGE,"E11")])]});
            var Q21;
            Q21=makeQuery(id+"F1.opExtrude","SWEPT_EDGE",EDGE,{"disambiguationData":[OSD([sQuery(id+"F0.wireOp",EDGE,"E9"),sQuery(id+"F0.wireOp",EDGE,"E10")])]});
            var Q22;
            Q22=makeQuery(id+"F1.opExtrude","SWEPT_EDGE",EDGE,{"disambiguationData":[OSD([sQuery(id+"F0.wireOp",EDGE,"E13"),sQuery(id+"F0.wireOp",EDGE,"E14")])]});
            var Q23;
            Q23=makeQuery(id+"F1.opExtrude","SWEPT_EDGE",EDGE,{"disambiguationData":[OSD([sQuery(id+"F0.wireOp",EDGE,"E14"),sQuery(id+"F0.wireOp",EDGE,"E15")])]});
            var Q24;
            Q24=makeQuery(id+"F1.opExtrude","SWEPT_EDGE",EDGE,{"disambiguationData":[OSD([sQuery(id+"F0.wireOp",EDGE,"E11"),sQuery(id+"F0.wireOp",EDGE,"E12")])]});
            var Q25;
            Q25=makeQuery(id+"F1.opExtrude","SWEPT_EDGE",EDGE,{"disambiguationData":[OSD([sQuery(id+"F0.wireOp",EDGE,"E12"),sQuery(id+"F0.wireOp",EDGE,"E13")])]});
            var Q26;
            Q26=makeQuery(id+"F1.opExtrude","SWEPT_EDGE",EDGE,{"disambiguationData":[OSD([sQuery(id+"F0.wireOp",EDGE,"E15"),sQuery(id+"F0.wireOp",EDGE,"E16")])]});
            var Q27;
            Q27=makeQuery(id+"F1.opExtrude","SWEPT_EDGE",EDGE,{"disambiguationData":[OSD([sQuery(id+"F0.wireOp",EDGE,"E17"),sQuery(id+"F0.wireOp",EDGE,"E18")])]});
            var Q28;
            Q28=makeQuery(id+"F1.opExtrude","SWEPT_EDGE",EDGE,{"disambiguationData":[OSD([sQuery(id+"F0.wireOp",EDGE,"E16"),sQuery(id+"F0.wireOp",EDGE,"E17")])]});
            var Q29;
            Q29=makeQuery(id+"F1.opExtrude","SWEPT_EDGE",EDGE,{"disambiguationData":[OSD([sQuery(id+"F0.wireOp",EDGE,"E19"),sQuery(id+"F0.wireOp",EDGE,"E20")])]});
            var Q30;
            Q30=makeQuery(id+"F1.opExtrude","SWEPT_EDGE",EDGE,{"disambiguationData":[OSD([sQuery(id+"F0.wireOp",EDGE,"E20"),sQuery(id+"F0.wireOp",EDGE,"E21")])]});
            var Q31;
            Q31=makeQuery(id+"F1.opExtrude","SWEPT_EDGE",EDGE,{"disambiguationData":[OSD([sQuery(id+"F0.wireOp",EDGE,"E21"),sQuery(id+"F0.wireOp",EDGE,"E22")])]});
            var Q32;
            Q32=makeQuery(id+"F1.opExtrude","SWEPT_EDGE",EDGE,{"disambiguationData":[OSD([sQuery(id+"F0.wireOp",EDGE,"E22"),sQuery(id+"F0.wireOp",EDGE,"E23")])]});
            var Q33;
            Q33=makeQuery(id+"F1.opExtrude","SWEPT_EDGE",EDGE,{"disambiguationData":[OSD([sQuery(id+"F0.wireOp",EDGE,"E23"),sQuery(id+"F0.wireOp",EDGE,"E24")])]});
            var Q34;
            Q34=makeQuery(id+"F1.opExtrude","SWEPT_EDGE",EDGE,{"disambiguationData":[OSD([sQuery(id+"F0.wireOp",EDGE,"E24"),sQuery(id+"F0.wireOp",EDGE,"E25")])]});
            var Q35;
            Q35=makeQuery(id+"F1.opExtrude","SWEPT_EDGE",EDGE,{"disambiguationData":[OSD([sQuery(id+"F0.wireOp",EDGE,"E25"),sQuery(id+"F0.wireOp",EDGE,"E26")])]});
            var Q36;
            Q36=makeQuery(id+"F1.opExtrude","SWEPT_EDGE",EDGE,{"disambiguationData":[OSD([sQuery(id+"F0.wireOp",EDGE,"E28"),sQuery(id+"F0.wireOp",EDGE,"E29")])]});
            var Q37;
            Q37=makeQuery(id+"F1.opExtrude","SWEPT_EDGE",EDGE,{"disambiguationData":[OSD([sQuery(id+"F0.wireOp",EDGE,"E29"),sQuery(id+"F0.wireOp",EDGE,"E30")])]});
            var Q38;
            Q38=makeQuery(id+"F1.opExtrude","SWEPT_EDGE",EDGE,{"disambiguationData":[OSD([sQuery(id+"F0.wireOp",EDGE,"E30"),sQuery(id+"F0.wireOp",EDGE,"E31")])]});
            var Q39;
            Q39=makeQuery(id+"F1.opExtrude","SWEPT_EDGE",EDGE,{"disambiguationData":[OSD([sQuery(id+"F0.wireOp",EDGE,"E33"),sQuery(id+"F0.wireOp",EDGE,"E35")])]});
            var Q40;
            Q40=makeQuery(id+"F1.opExtrude","SWEPT_EDGE",EDGE,{"disambiguationData":[OSD([sQuery(id+"F0.wireOp",EDGE,"E32"),sQuery(id+"F0.wireOp",EDGE,"E33")])]});
            var Q41;
            Q41=makeQuery(id+"F1.opExtrude","SWEPT_EDGE",EDGE,{"disambiguationData":[OSD([sQuery(id+"F0.wireOp",EDGE,"E35"),sQuery(id+"F0.wireOp",EDGE,"E36")])]});
            var Q42;
            Q42=makeQuery(id+"F1.opExtrude","SWEPT_EDGE",EDGE,{"disambiguationData":[OSD([sQuery(id+"F0.wireOp",EDGE,"E36"),sQuery(id+"F0.wireOp",EDGE,"E37")])]});
            var Q43;
            Q43=makeQuery(id+"F1.opExtrude","SWEPT_EDGE",EDGE,{"disambiguationData":[OSD([sQuery(id+"F0.wireOp",EDGE,"E39"),sQuery(id+"F0.wireOp",EDGE,"E40")])]});
            var Q44;
            Q44=makeQuery(id+"F1.opExtrude","SWEPT_EDGE",EDGE,{"disambiguationData":[OSD([sQuery(id+"F0.wireOp",EDGE,"E40"),sQuery(id+"F0.wireOp",EDGE,"E41")])]});
            var Q45;
            Q45=makeQuery(id+"F1.opExtrude","SWEPT_EDGE",EDGE,{"disambiguationData":[OSD([sQuery(id+"F0.wireOp",EDGE,"E42"),sQuery(id+"F0.wireOp",EDGE,"E43")])]});
            var Q46;
            Q46=makeQuery(id+"F1.opExtrude","SWEPT_EDGE",EDGE,{"disambiguationData":[OSD([sQuery(id+"F0.wireOp",EDGE,"E41"),sQuery(id+"F0.wireOp",EDGE,"E42")])]});
            var Q47;
            Q47=makeQuery(id+"F1.opExtrude","SWEPT_EDGE",EDGE,{"disambiguationData":[OSD([sQuery(id+"F0.wireOp",EDGE,"E43"),sQuery(id+"F0.wireOp",EDGE,"E44")])]});
            var Q48;
            Q48=makeQuery(id+"F1.opExtrude","SWEPT_EDGE",EDGE,{"disambiguationData":[OSD([sQuery(id+"F0.wireOp",EDGE,"E46"),sQuery(id+"F0.wireOp",EDGE,"E47")])]});
            var Q49;
            Q49=makeQuery(id+"F1.opExtrude","SWEPT_EDGE",EDGE,{"disambiguationData":[OSD([sQuery(id+"F0.wireOp",EDGE,"E47"),sQuery(id+"F0.wireOp",EDGE,"E48")])]});
            var Q50;
            Q50=makeQuery(id+"F1.opExtrude","SWEPT_EDGE",EDGE,{"disambiguationData":[OSD([sQuery(id+"F0.wireOp",EDGE,"E38"),sQuery(id+"F0.wireOp",EDGE,"E39")])]});
            var Q51;
            Q51=makeQuery(id+"F1.opExtrude","SWEPT_EDGE",EDGE,{"disambiguationData":[OSD([sQuery(id+"F0.wireOp",EDGE,"E45"),sQuery(id+"F0.wireOp",EDGE,"E46")])]});
            var Q52;
            Q52=makeQuery(id+"F1.opExtrude","SWEPT_EDGE",EDGE,{"disambiguationData":[OSD([sQuery(id+"F0.wireOp",EDGE,"E48"),sQuery(id+"F0.wireOp",EDGE,"E49")])]});
            var Q53;
            Q53=makeQuery(id+"F1.opExtrude","SWEPT_EDGE",EDGE,{"disambiguationData":[OSD([sQuery(id+"F0.wireOp",EDGE,"E49"),sQuery(id+"F0.wireOp",EDGE,"E50")])]});
            var Q54;
            Q54=makeQuery(id+"F1.opExtrude","SWEPT_EDGE",EDGE,{"disambiguationData":[OSD([sQuery(id+"F0.wireOp",EDGE,"E52"),sQuery(id+"F0.wireOp",EDGE,"E53")])]});
            var Q55;
            Q55=makeQuery(id+"F1.opExtrude","SWEPT_EDGE",EDGE,{"disambiguationData":[OSD([sQuery(id+"F0.wireOp",EDGE,"E53"),sQuery(id+"F0.wireOp",EDGE,"E54")])]});
            var Q56;
            Q56=makeQuery(id+"F1.opExtrude","SWEPT_EDGE",EDGE,{"disambiguationData":[OSD([sQuery(id+"F0.wireOp",EDGE,"E54"),sQuery(id+"F0.wireOp",EDGE,"E55")])]});
            var Q57;
            Q57=makeQuery(id+"F1.opExtrude","SWEPT_EDGE",EDGE,{"disambiguationData":[OSD([sQuery(id+"F0.wireOp",EDGE,"E55"),sQuery(id+"F0.wireOp",EDGE,"E56")])]});
            var Q58;
            Q58=makeQuery(id+"F1.opExtrude","SWEPT_EDGE",EDGE,{"disambiguationData":[OSD([sQuery(id+"F0.wireOp",EDGE,"E56"),sQuery(id+"F0.wireOp",EDGE,"E133")])]});
            var Q59;
            Q59=makeQuery(id+"F1.opExtrude","SWEPT_EDGE",EDGE,{"disambiguationData":[OSD([sQuery(id+"F0.wireOp",EDGE,"E84"),sQuery(id+"F0.wireOp",EDGE,"E133")])]});
            var Q60;
            Q60=makeQuery(id+"F1.opExtrude","SWEPT_EDGE",EDGE,{"disambiguationData":[OSD([sQuery(id+"F0.wireOp",EDGE,"E85"),sQuery(id+"F0.wireOp",EDGE,"E86")])]});
            var Q61;
            Q61=makeQuery(id+"F1.opExtrude","SWEPT_EDGE",EDGE,{"disambiguationData":[OSD([sQuery(id+"F0.wireOp",EDGE,"E84"),sQuery(id+"F0.wireOp",EDGE,"E85")])]});
            var Q62;
            Q62=makeQuery(id+"F1.opExtrude","SWEPT_EDGE",EDGE,{"disambiguationData":[OSD([sQuery(id+"F0.wireOp",EDGE,"E87"),sQuery(id+"F0.wireOp",EDGE,"E88")])]});
            var Q63;
            Q63=makeQuery(id+"F1.opExtrude","SWEPT_EDGE",EDGE,{"disambiguationData":[OSD([sQuery(id+"F0.wireOp",EDGE,"E86"),sQuery(id+"F0.wireOp",EDGE,"E87")])]});
            var Q64;
            Q64=makeQuery(id+"F1.opExtrude","SWEPT_EDGE",EDGE,{"disambiguationData":[OSD([sQuery(id+"F0.wireOp",EDGE,"E88"),sQuery(id+"F0.wireOp",EDGE,"E89")])]});
            var Q65;
            Q65=makeQuery(id+"F1.opExtrude","SWEPT_EDGE",EDGE,{"disambiguationData":[OSD([sQuery(id+"F0.wireOp",EDGE,"E89"),sQuery(id+"F0.wireOp",EDGE,"E90")])]});
            var Q66;
            Q66=makeQuery(id+"F1.opExtrude","SWEPT_EDGE",EDGE,{"disambiguationData":[OSD([sQuery(id+"F0.wireOp",EDGE,"E90"),sQuery(id+"F0.wireOp",EDGE,"E91")])]});
            var Q67;
            Q67=makeQuery(id+"F1.opExtrude","SWEPT_EDGE",EDGE,{"disambiguationData":[OSD([sQuery(id+"F0.wireOp",EDGE,"E91"),sQuery(id+"F0.wireOp",EDGE,"E92")])]});
            var Q68;
            Q68=makeQuery(id+"F1.opExtrude","SWEPT_EDGE",EDGE,{"disambiguationData":[OSD([sQuery(id+"F0.wireOp",EDGE,"E92"),sQuery(id+"F0.wireOp",EDGE,"E93")])]});
            var Q69;
            Q69=makeQuery(id+"F1.opExtrude","SWEPT_EDGE",EDGE,{"disambiguationData":[OSD([sQuery(id+"F0.wireOp",EDGE,"E93"),sQuery(id+"F0.wireOp",EDGE,"E94")])]});
            var Q70;
            Q70=makeQuery(id+"F1.opExtrude","SWEPT_EDGE",EDGE,{"disambiguationData":[OSD([sQuery(id+"F0.wireOp",EDGE,"E96"),sQuery(id+"F0.wireOp",EDGE,"E97")])]});
            var Q71;
            Q71=makeQuery(id+"F1.opExtrude","SWEPT_EDGE",EDGE,{"disambiguationData":[OSD([sQuery(id+"F0.wireOp",EDGE,"E95"),sQuery(id+"F0.wireOp",EDGE,"E96")])]});
            var Q72;
            Q72=makeQuery(id+"F1.opExtrude","SWEPT_EDGE",EDGE,{"disambiguationData":[OSD([sQuery(id+"F0.wireOp",EDGE,"E94"),sQuery(id+"F0.wireOp",EDGE,"E95")])]});
            var Q73;
            Q73=makeQuery(id+"F1.opExtrude","SWEPT_EDGE",EDGE,{"disambiguationData":[OSD([sQuery(id+"F0.wireOp",EDGE,"E101"),sQuery(id+"F0.wireOp",EDGE,"E102")])]});
            var Q74;
            Q74=makeQuery(id+"F1.opExtrude","SWEPT_EDGE",EDGE,{"disambiguationData":[OSD([sQuery(id+"F0.wireOp",EDGE,"E99"),sQuery(id+"F0.wireOp",EDGE,"E100")])]});
            var Q75;
            Q75=makeQuery(id+"F1.opExtrude","SWEPT_EDGE",EDGE,{"disambiguationData":[OSD([sQuery(id+"F0.wireOp",EDGE,"E97"),sQuery(id+"F0.wireOp",EDGE,"E98")])]});
            var Q76;
            Q76=makeQuery(id+"F1.opExtrude","SWEPT_EDGE",EDGE,{"disambiguationData":[OSD([sQuery(id+"F0.wireOp",EDGE,"E103"),sQuery(id+"F0.wireOp",EDGE,"E104")])]});
            var Q77;
            Q77=makeQuery(id+"F1.opExtrude","SWEPT_EDGE",EDGE,{"disambiguationData":[OSD([sQuery(id+"F0.wireOp",EDGE,"E104"),sQuery(id+"F0.wireOp",EDGE,"E105")])]});
            var Q78;
            Q78=makeQuery(id+"F1.opExtrude","SWEPT_EDGE",EDGE,{"disambiguationData":[OSD([sQuery(id+"F0.wireOp",EDGE,"E105"),sQuery(id+"F0.wireOp",EDGE,"E106")])]});
            var Q79;
            Q79=makeQuery(id+"F1.opExtrude","SWEPT_EDGE",EDGE,{"disambiguationData":[OSD([sQuery(id+"F0.wireOp",EDGE,"E107"),sQuery(id+"F0.wireOp",EDGE,"E108")])]});
            var Q80;
            Q80=makeQuery(id+"F1.opExtrude","SWEPT_EDGE",EDGE,{"disambiguationData":[OSD([sQuery(id+"F0.wireOp",EDGE,"E108"),sQuery(id+"F0.wireOp",EDGE,"E109")])]});
            var Q81;
            Q81=makeQuery(id+"F1.opExtrude","SWEPT_EDGE",EDGE,{"disambiguationData":[OSD([sQuery(id+"F0.wireOp",EDGE,"E109"),sQuery(id+"F0.wireOp",EDGE,"E110")])]});
            var Q82;
            Q82=makeQuery(id+"F1.opExtrude","SWEPT_EDGE",EDGE,{"disambiguationData":[OSD([sQuery(id+"F0.wireOp",EDGE,"E110"),sQuery(id+"F0.wireOp",EDGE,"E111")])]});
            var Q83;
            Q83=makeQuery(id+"F1.opExtrude","SWEPT_EDGE",EDGE,{"disambiguationData":[OSD([sQuery(id+"F0.wireOp",EDGE,"E116"),sQuery(id+"F0.wireOp",EDGE,"E117")])]});
            var Q84;
            Q84=makeQuery(id+"F1.opExtrude","SWEPT_EDGE",EDGE,{"disambiguationData":[OSD([sQuery(id+"F0.wireOp",EDGE,"E115"),sQuery(id+"F0.wireOp",EDGE,"E116")])]});
            var Q85;
            Q85=makeQuery(id+"F1.opExtrude","SWEPT_EDGE",EDGE,{"disambiguationData":[OSD([sQuery(id+"F0.wireOp",EDGE,"E114"),sQuery(id+"F0.wireOp",EDGE,"E115")])]});
            var Q86;
            Q86=makeQuery(id+"F1.opExtrude","SWEPT_EDGE",EDGE,{"disambiguationData":[OSD([sQuery(id+"F0.wireOp",EDGE,"E18"),sQuery(id+"F0.wireOp",EDGE,"E19")])]});
            var Q87;
            Q87=makeQuery(id+"F1.opExtrude","SWEPT_EDGE",EDGE,{"disambiguationData":[OSD([sQuery(id+"F0.wireOp",EDGE,"03a7d401-13a4-461c-8d26-49e58f535fc3"),sQuery(id+"F0.wireOp",EDGE,"a3bd3416-707c-4540-b944-4694eed28f36")])]});
            var Q88;
            Q88=makeQuery(id+"F1.opExtrude","SWEPT_EDGE",EDGE,{"disambiguationData":[OSD([sQuery(id+"F0.wireOp",EDGE,"a728134e-6b61-4dc4-b5d7-6c3bc719696b"),sQuery(id+"F0.wireOp",EDGE,"03a7d401-13a4-461c-8d26-49e58f535fc3")])]});
            var Q89;
            Q89=makeQuery(id+"F1.opExtrude","SWEPT_EDGE",EDGE,{"disambiguationData":[OSD([sQuery(id+"F0.wireOp",EDGE,"97e02e69-64ad-4fc2-ba99-ada5d7f4203f"),sQuery(id+"F0.wireOp",EDGE,"a728134e-6b61-4dc4-b5d7-6c3bc719696b")])]});
            var Q90;
            Q90=makeQuery(id+"F1.opExtrude","SWEPT_EDGE",EDGE,{"disambiguationData":[OSD([sQuery(id+"F0.wireOp",EDGE,"6c9cf376-8706-417d-a2f8-7997adb0d334"),sQuery(id+"F0.wireOp",EDGE,"4fed2303-0bfb-4ab1-8d0b-459c1d0f22cc")])]});
            var Q91;
            Q91=makeQuery(id+"F1.opExtrude","SWEPT_EDGE",EDGE,{"disambiguationData":[OSD([sQuery(id+"F0.wireOp",EDGE,"d8a8be79-a09e-4068-9526-32c7dd8d4367"),sQuery(id+"F0.wireOp",EDGE,"6c9cf376-8706-417d-a2f8-7997adb0d334")])]});
            var Q92;
            Q92=makeQuery(id+"F1.opExtrude","SWEPT_EDGE",EDGE,{"disambiguationData":[OSD([sQuery(id+"F0.wireOp",EDGE,"c1167789-1dd6-4c8a-b9db-14aab257ee89"),sQuery(id+"F0.wireOp",EDGE,"97e02e69-64ad-4fc2-ba99-ada5d7f4203f")])]});
            var Q93;
            Q93=makeQuery(id+"F1.opExtrude","SWEPT_EDGE",EDGE,{"disambiguationData":[OSD([sQuery(id+"F0.wireOp",EDGE,"24c02880-417f-4c24-b8b8-f4173c506c8a"),sQuery(id+"F0.wireOp",EDGE,"c1167789-1dd6-4c8a-b9db-14aab257ee89")])]});
            var Q94;
            Q94=makeQuery(id+"F1.opExtrude","SWEPT_EDGE",EDGE,{"disambiguationData":[OSD([sQuery(id+"F0.wireOp",EDGE,"24c02880-417f-4c24-b8b8-f4173c506c8a"),sQuery(id+"F0.wireOp",EDGE,"767a3e55-a90d-4037-a153-983baa27fcb7")])]});
            var Q95;
            Q95=makeQuery(id+"F1.opExtrude","SWEPT_EDGE",EDGE,{"disambiguationData":[OSD([sQuery(id+"F0.wireOp",EDGE,"4fed2303-0bfb-4ab1-8d0b-459c1d0f22cc"),sQuery(id+"F0.wireOp",EDGE,"54fe9d9b-3ee6-47e4-8d7e-fb489f7f2c80")])]});
            var Q96;
            Q96=makeQuery(id+"F1.opExtrude","SWEPT_EDGE",EDGE,{"disambiguationData":[OSD([sQuery(id+"F0.wireOp",EDGE,"E119"),sQuery(id+"F0.wireOp",EDGE,"E120")])]});
            var Q97;
            Q97=makeQuery(id+"F1.opExtrude","SWEPT_EDGE",EDGE,{"disambiguationData":[OSD([sQuery(id+"F0.wireOp",EDGE,"E117"),sQuery(id+"F0.wireOp",EDGE,"E118")])]});
            var Q98;
            Q98=makeQuery(id+"F1.opExtrude","SWEPT_EDGE",EDGE,{"disambiguationData":[OSD([sQuery(id+"F0.wireOp",EDGE,"E121"),sQuery(id+"F0.wireOp",EDGE,"E122")])]});
            var Q99;
            Q99=makeQuery(id+"F1.opExtrude","SWEPT_EDGE",EDGE,{"disambiguationData":[OSD([sQuery(id+"F0.wireOp",EDGE,"E120"),sQuery(id+"F0.wireOp",EDGE,"E121")])]});
            var Q100;
            Q100=makeQuery(id+"F1.opExtrude","SWEPT_EDGE",EDGE,{"disambiguationData":[OSD([sQuery(id+"F0.wireOp",EDGE,"E122"),sQuery(id+"F0.wireOp",EDGE,"E123")])]});
            var Q101;
            Q101=makeQuery(id+"F1.opExtrude","SWEPT_EDGE",EDGE,{"disambiguationData":[OSD([sQuery(id+"F0.wireOp",EDGE,"E123"),sQuery(id+"F0.wireOp",EDGE,"E124")])]});
            var Q102;
            Q102=makeQuery(id+"F1.opExtrude","SWEPT_EDGE",EDGE,{"disambiguationData":[OSD([sQuery(id+"F0.wireOp",EDGE,"E8"),sQuery(id+"F0.wireOp",EDGE,"E9")])]});
            var Q103;
            Q103=makeQuery(id+"F1.opExtrude","SWEPT_EDGE",EDGE,{"disambiguationData":[OSD([sQuery(id+"F0.wireOp",EDGE,"E126"),sQuery(id+"F0.wireOp",EDGE,"E127")])]});
            var Q104;
            Q104=makeQuery(id+"F1.opExtrude","SWEPT_EDGE",EDGE,{"disambiguationData":[OSD([sQuery(id+"F0.wireOp",EDGE,"E83"),sQuery(id+"F0.wireOp",EDGE,"E132")])]});
            fillet(context, id + "F4", {"entities" : qUnion([Q0, Q1, Q2, Q3, Q4, Q5, Q6, Q7, Q8, Q9, Q10, Q11, Q12, Q13, Q14, Q15, Q16, Q17, Q18, Q19, Q20, Q21, Q22, Q23, Q24, Q25, Q26, Q27, Q28, Q29, Q30, Q31, Q32, Q33, Q34, Q35, Q36, Q37, Q38, Q39, Q40, Q41, Q42, Q43, Q44, Q45, Q46, Q47, Q48, Q49, Q50, Q51, Q52, Q53, Q54, Q55, Q56, Q57, Q58, Q59, Q60, Q61, Q62, Q63, Q64, Q65, Q66, Q67, Q68, Q69, Q70, Q71, Q72, Q73, Q74, Q75, Q76, Q77, Q78, Q79, Q80, Q81, Q82, Q83, Q84, Q85, Q86, Q87, Q88, Q89, Q90, Q91, Q92, Q93, Q94, Q95, Q96, Q97, Q98, Q99, Q100, Q101, Q102, Q103, Q104]), "radius" : .6 * mm, "tangentPropagation" : true, "allowEdgeOverflow" : false});
        }
    });
